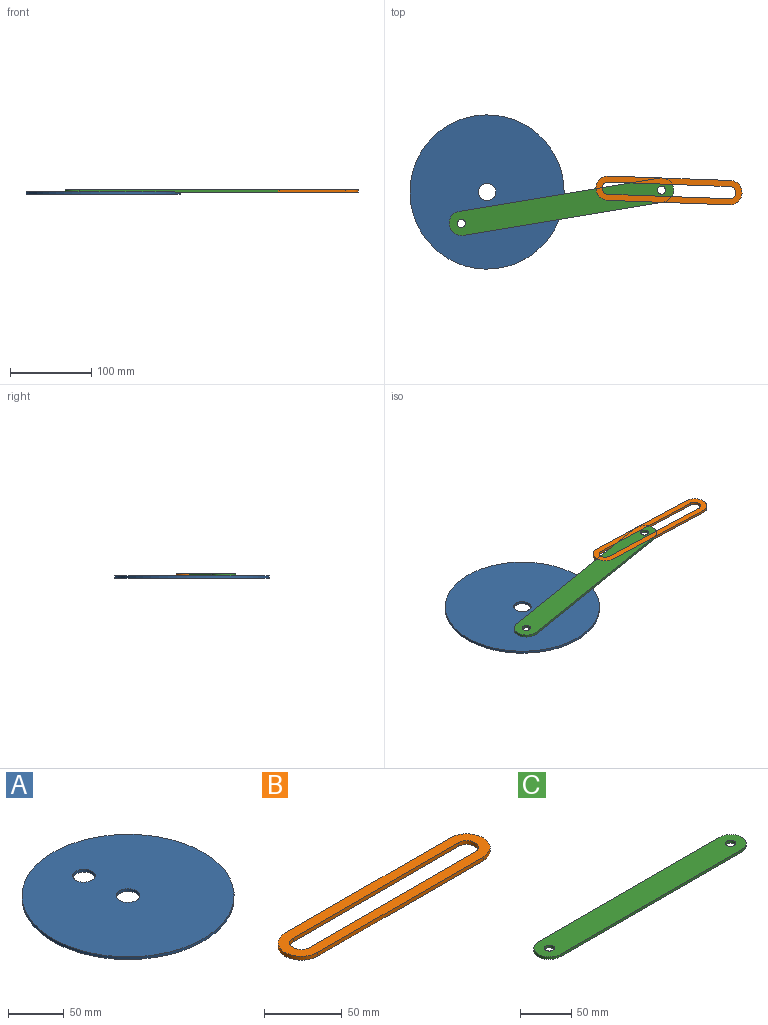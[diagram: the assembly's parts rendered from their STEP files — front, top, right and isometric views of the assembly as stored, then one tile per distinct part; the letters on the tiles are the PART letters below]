
ASSEMBLY  parts=3 mates=2
PART A: 5 faces, bbox 190x190x3 mm
  f0: cylinder r=10mm len=20mm, axis (0,0,-1), area 188.5mm2, adj f3,f4
  f1: cylinder r=10.64mm len=21.28mm, axis (0,0,-1), area 200.6mm2, adj f3,f4
  f2: cylinder r=95mm len=190mm, axis (0,0,-1), area 1790.7mm2, adj f3,f4
  f3: plane 190x190mm, normal (0,0,1), area 27682.9mm2, adj f0,f1,f2
  f4: plane 190x190mm, normal (0,0,-1), area 27682.9mm2, adj f0,f1,f2
PART B: 10 faces, bbox 180x30x3 mm
  f0: cylinder r=15mm len=30mm, axis (0,0,-1), area 141.4mm2, adj f1,f7,f8,f9
  f1: plane 150x3mm, normal (0,-1,0), area 450mm2, adj f0,f2,f8,f9
  f2: cylinder r=15mm len=30mm, axis (0,0,-1), area 141.4mm2, adj f1,f7,f8,f9
  f3: plane 150x3mm, normal (0,1,0), area 450mm2, adj f4,f6,f8,f9
  f4: cylinder r=7.5mm len=15mm, axis (0,0,-1), area 70.7mm2, adj f3,f5,f8,f9
  f5: plane 150x3mm, normal (0,-1,0), area 450mm2, adj f4,f6,f8,f9
  f6: cylinder r=7.5mm len=15mm, axis (0,0,-1), area 70.7mm2, adj f3,f5,f8,f9
  f7: plane 150x3mm, normal (0,1,0), area 450mm2, adj f0,f2,f8,f9
  f8: plane 180x30mm, normal (0,0,1), area 2780.1mm2, adj f0,f1,f2,f3,f4,f5,f6,f7
  f9: plane 180x30mm, normal (0,0,-1), area 2780.1mm2, adj f0,f1,f2,f3,f4,f5,f6,f7
PART C: 8 faces, bbox 280x30x3 mm
  f0: cylinder r=15mm len=30mm, axis (0,0,-1), area 141.4mm2, adj f1,f5,f6,f7
  f1: plane 250x3mm, normal (0,-1,0), area 750mm2, adj f0,f2,f6,f7
  f2: cylinder r=15mm len=30mm, axis (0,0,-1), area 141.4mm2, adj f1,f5,f6,f7
  f3: cylinder r=5mm len=10mm, axis (0,0,-1), area 94.2mm2, adj f6,f7
  f4: cylinder r=5mm len=10mm, axis (0,0,-1), area 94.2mm2, adj f6,f7
  f5: plane 250x3mm, normal (0,1,0), area 750mm2, adj f0,f2,f6,f7
  f6: plane 280x30mm, normal (0,0,1), area 8049.8mm2, adj f0,f1,f2,f3,f4,f5
  f7: plane 280x30mm, normal (0,0,-1), area 8049.8mm2, adj f0,f1,f2,f3,f4,f5
PLACE A rot(axis=(0,0,1),133.6deg) t=(0,0,-3)mm
PLACE B rot(axis=(0,0,-1),2.1deg) t=(224.6,1.94,0)mm fixed
PLACE C rot(axis=(0,0,1),9.4deg) t=(55.92,-24.12,0)mm
MATE revolute C.f0 <-> A.f0  axis (0,0,-1) through (-31.69,-38.67,0)mm
MATE pin_slot C.f2 <-> B.f8  axis (0,0,1) through (214.93,2.3,3)mm
